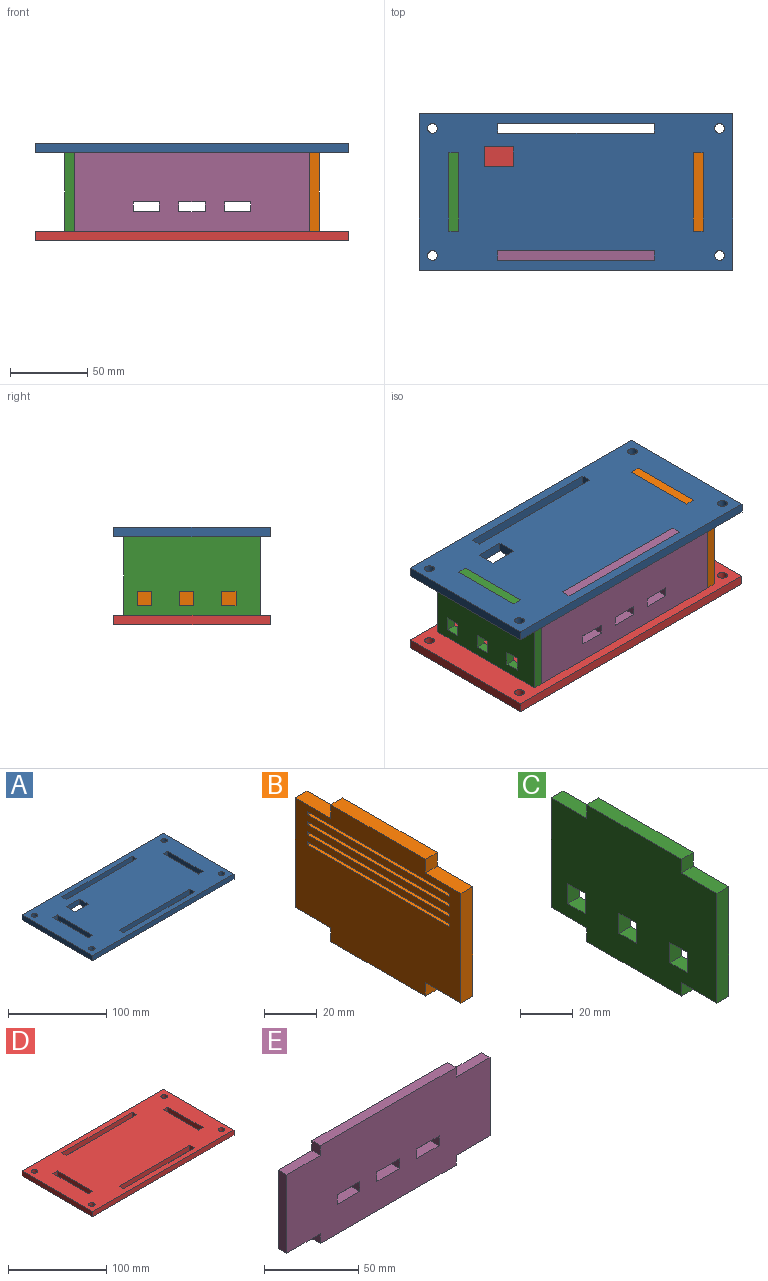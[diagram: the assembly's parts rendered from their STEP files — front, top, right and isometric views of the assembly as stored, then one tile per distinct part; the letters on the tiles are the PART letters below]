
ASSEMBLY  parts=5 mates=4
PART A: 30 faces, bbox 203.2x101.6x6.4 mm
  f0: plane 6.35x6.35mm, normal (0,-1,0), area 40.3mm2, adj f1,f27,f28,f29
  f1: plane 50.8x6.35mm, normal (-1,0,0), area 322.6mm2, adj f0,f2,f28,f29
  f2: plane 6.35x6.35mm, normal (0,1,0), area 40.3mm2, adj f1,f27,f28,f29
  f3: plane 101.6x6.35mm, normal (0,-1,0), area 645.2mm2, adj f4,f18,f28,f29
  f4: plane 6.35x6.35mm, normal (-1,0,0), area 40.3mm2, adj f3,f5,f28,f29
  f5: plane 101.6x6.35mm, normal (0,1,0), area 645.2mm2, adj f4,f18,f28,f29
  f6: plane 12.7x6.35mm, normal (1,0,0), area 80.6mm2, adj f7,f23,f28,f29
  f7: plane 19.05x6.35mm, normal (0,-1,0), area 121mm2, adj f6,f8,f28,f29
  f8: plane 12.7x6.35mm, normal (-1,0,0), area 80.6mm2, adj f7,f23,f28,f29
  f9: plane 6.35x6.35mm, normal (1,0,0), area 40.3mm2, adj f10,f24,f28,f29
  f10: plane 101.6x6.35mm, normal (0,-1,0), area 645.2mm2, adj f9,f11,f28,f29
  f11: plane 6.35x6.35mm, normal (-1,0,0), area 40.3mm2, adj f10,f24,f28,f29
  f12: plane 50.8x6.35mm, normal (1,0,0), area 322.6mm2, adj f13,f25,f28,f29
  f13: plane 6.35x6.35mm, normal (0,-1,0), area 40.3mm2, adj f12,f14,f28,f29
  f14: plane 50.8x6.35mm, normal (-1,0,0), area 322.6mm2, adj f13,f25,f28,f29
  f15: plane 101.6x6.35mm, normal (-1,0,0), area 645.2mm2, adj f16,f26,f28,f29
  f16: plane 203.2x6.35mm, normal (0,-1,0), area 1290.3mm2, adj f15,f17,f28,f29
  f17: plane 101.6x6.35mm, normal (1,0,0), area 645.2mm2, adj f16,f26,f28,f29
  f18: plane 6.35x6.35mm, normal (1,0,0), area 40.3mm2, adj f3,f5,f28,f29
  f19: cylinder r=3.17mm len=6.35mm, axis (0,0,-1), area 126.7mm2, adj f28,f29
  f20: cylinder r=3.17mm len=6.35mm, axis (0,0,-1), area 126.7mm2, adj f28,f29
  f21: cylinder r=3.17mm len=6.35mm, axis (0,0,-1), area 126.7mm2, adj f28,f29
  f22: cylinder r=3.17mm len=6.35mm, axis (0,0,-1), area 126.7mm2, adj f28,f29
  f23: plane 19.05x6.35mm, normal (0,1,0), area 121mm2, adj f6,f8,f28,f29
  f24: plane 101.6x6.35mm, normal (0,1,0), area 645.2mm2, adj f9,f11,f28,f29
  f25: plane 6.35x6.35mm, normal (0,1,0), area 40.3mm2, adj f12,f14,f28,f29
  f26: plane 203.2x6.35mm, normal (0,1,0), area 1290.3mm2, adj f15,f17,f28,f29
  f27: plane 50.8x6.35mm, normal (1,0,0), area 322.6mm2, adj f0,f2,f28,f29
  f28: plane 203.2x101.6mm, normal (0,0,1), area 18341mm2, adj f0,f1,f2,f3,f4,f5,f6,f7
  f29: plane 203.2x101.6mm, normal (0,0,-1), area 18341mm2, adj f0,f1,f2,f3,f4,f5,f6,f7
PART B: 30 faces, bbox 6.4x88.9x63.5 mm
  f0: plane 50.8x6.35mm, normal (0,-1,0), area 322.6mm2, adj f1,f27,f28,f29
  f1: plane 19.05x6.35mm, normal (0,0,-1), area 121mm2, adj f0,f2,f28,f29
  f2: plane 6.35x6.35mm, normal (0,-1,0), area 40.3mm2, adj f1,f3,f28,f29
  f3: plane 50.8x6.35mm, normal (0,0,-1), area 322.6mm2, adj f2,f4,f28,f29
  f4: plane 6.35x6.35mm, normal (0,1,0), area 40.3mm2, adj f3,f5,f28,f29
  f5: plane 19.05x6.35mm, normal (0,0,-1), area 121mm2, adj f4,f6,f28,f29
  f6: plane 50.8x6.35mm, normal (0,1,0), area 322.6mm2, adj f5,f7,f28,f29
  f7: plane 19.05x6.35mm, normal (0,0,1), area 121mm2, adj f6,f8,f28,f29
  f8: plane 6.35x6.35mm, normal (0,1,0), area 40.3mm2, adj f7,f9,f28,f29
  f9: plane 50.8x6.35mm, normal (0,0,1), area 322.6mm2, adj f8,f10,f28,f29
  f10: plane 6.35x6.35mm, normal (0,-1,0), area 40.3mm2, adj f9,f27,f28,f29
  f11: plane 6.35x1.5mm, normal (0,1,0), area 9.5mm2, adj f12,f23,f28,f29
  f12: plane 76.2x6.35mm, normal (0,0,-1), area 483.9mm2, adj f11,f13,f28,f29
  f13: plane 6.35x1.5mm, normal (0,-1,0), area 9.5mm2, adj f12,f23,f28,f29
  f14: plane 6.35x1.5mm, normal (0,1,0), area 9.5mm2, adj f15,f24,f28,f29
  f15: plane 76.2x6.35mm, normal (0,0,-1), area 483.9mm2, adj f14,f16,f28,f29
  f16: plane 6.35x1.5mm, normal (0,-1,0), area 9.5mm2, adj f15,f24,f28,f29
  f17: plane 6.35x1.5mm, normal (0,1,0), area 9.5mm2, adj f18,f25,f28,f29
  f18: plane 76.2x6.35mm, normal (0,0,-1), area 483.9mm2, adj f17,f19,f28,f29
  f19: plane 6.35x1.5mm, normal (0,-1,0), area 9.5mm2, adj f18,f25,f28,f29
  f20: plane 6.35x1.5mm, normal (0,1,0), area 9.5mm2, adj f21,f26,f28,f29
  f21: plane 76.2x6.35mm, normal (0,0,-1), area 483.9mm2, adj f20,f22,f28,f29
  f22: plane 6.35x1.5mm, normal (0,-1,0), area 9.5mm2, adj f21,f26,f28,f29
  f23: plane 76.2x6.35mm, normal (0,0,1), area 483.9mm2, adj f11,f13,f28,f29
  f24: plane 76.2x6.35mm, normal (0,0,1), area 483.9mm2, adj f14,f16,f28,f29
  f25: plane 76.2x6.35mm, normal (0,0,1), area 483.9mm2, adj f17,f19,f28,f29
  f26: plane 76.2x6.35mm, normal (0,0,1), area 483.9mm2, adj f20,f22,f28,f29
  f27: plane 19.05x6.35mm, normal (0,0,1), area 121mm2, adj f0,f10,f28,f29
  f28: plane 88.9x63.5mm, normal (-1,0,0), area 4705.6mm2, adj f0,f1,f2,f3,f4,f5,f6,f7
  f29: plane 88.9x63.5mm, normal (1,0,0), area 4705.6mm2, adj f0,f1,f2,f3,f4,f5,f6,f7
PART C: 26 faces, bbox 6.4x88.9x63.5 mm
  f0: plane 6.35x6.35mm, normal (0,1,0), area 40.3mm2, adj f1,f23,f24,f25
  f1: plane 50.8x6.35mm, normal (0,0,1), area 322.6mm2, adj f0,f2,f24,f25
  f2: plane 6.35x6.35mm, normal (0,-1,0), area 40.3mm2, adj f1,f3,f24,f25
  f3: plane 19.05x6.35mm, normal (0,0,1), area 121mm2, adj f2,f4,f24,f25
  f4: plane 50.8x6.35mm, normal (0,-1,0), area 322.6mm2, adj f3,f5,f24,f25
  f5: plane 19.05x6.35mm, normal (0,0,-1), area 121mm2, adj f4,f6,f24,f25
  f6: plane 6.35x6.35mm, normal (0,-1,0), area 40.3mm2, adj f5,f7,f24,f25
  f7: plane 50.8x6.35mm, normal (0,0,-1), area 322.6mm2, adj f6,f8,f24,f25
  f8: plane 6.35x6.35mm, normal (0,1,0), area 40.3mm2, adj f7,f9,f24,f25
  f9: plane 19.05x6.35mm, normal (0,0,-1), area 121mm2, adj f8,f10,f24,f25
  f10: plane 50.8x6.35mm, normal (0,1,0), area 322.6mm2, adj f9,f23,f24,f25
  f11: plane 9.38x6.35mm, normal (0,0,-1), area 59.6mm2, adj f12,f20,f24,f25
  f12: plane 9.38x6.35mm, normal (0,-1,0), area 59.6mm2, adj f11,f13,f24,f25
  f13: plane 9.38x6.35mm, normal (0,0,1), area 59.6mm2, adj f12,f20,f24,f25
  f14: plane 9.38x6.35mm, normal (0,0,-1), area 59.6mm2, adj f15,f21,f24,f25
  f15: plane 9.38x6.35mm, normal (0,-1,0), area 59.6mm2, adj f14,f16,f24,f25
  f16: plane 9.38x6.35mm, normal (0,0,1), area 59.6mm2, adj f15,f21,f24,f25
  f17: plane 9.38x6.35mm, normal (0,0,-1), area 59.6mm2, adj f18,f22,f24,f25
  f18: plane 9.38x6.35mm, normal (0,-1,0), area 59.6mm2, adj f17,f19,f24,f25
  f19: plane 9.38x6.35mm, normal (0,0,1), area 59.6mm2, adj f18,f22,f24,f25
  f20: plane 9.38x6.35mm, normal (0,1,0), area 59.6mm2, adj f11,f13,f24,f25
  f21: plane 9.38x6.35mm, normal (0,1,0), area 59.6mm2, adj f14,f16,f24,f25
  f22: plane 9.38x6.35mm, normal (0,1,0), area 59.6mm2, adj f17,f19,f24,f25
  f23: plane 19.05x6.35mm, normal (0,0,1), area 121mm2, adj f0,f10,f24,f25
  f24: plane 88.9x63.5mm, normal (1,0,0), area 4897.4mm2, adj f0,f1,f2,f3,f4,f5,f6,f7
  f25: plane 88.9x63.5mm, normal (-1,0,0), area 4897.4mm2, adj f0,f1,f2,f3,f4,f5,f6,f7
PART D: 26 faces, bbox 203.2x101.6x6.4 mm
  f0: plane 6.35x6.35mm, normal (0,-1,0), area 40.3mm2, adj f1,f23,f24,f25
  f1: plane 50.8x6.35mm, normal (-1,0,0), area 322.6mm2, adj f0,f2,f24,f25
  f2: plane 6.35x6.35mm, normal (0,1,0), area 40.3mm2, adj f1,f23,f24,f25
  f3: plane 101.6x6.35mm, normal (0,-1,0), area 645.2mm2, adj f4,f15,f24,f25
  f4: plane 6.35x6.35mm, normal (-1,0,0), area 40.3mm2, adj f3,f5,f24,f25
  f5: plane 101.6x6.35mm, normal (0,1,0), area 645.2mm2, adj f4,f15,f24,f25
  f6: plane 6.35x6.35mm, normal (1,0,0), area 40.3mm2, adj f7,f20,f24,f25
  f7: plane 101.6x6.35mm, normal (0,-1,0), area 645.2mm2, adj f6,f8,f24,f25
  f8: plane 6.35x6.35mm, normal (-1,0,0), area 40.3mm2, adj f7,f20,f24,f25
  f9: plane 50.8x6.35mm, normal (1,0,0), area 322.6mm2, adj f10,f21,f24,f25
  f10: plane 6.35x6.35mm, normal (0,-1,0), area 40.3mm2, adj f9,f11,f24,f25
  f11: plane 50.8x6.35mm, normal (-1,0,0), area 322.6mm2, adj f10,f21,f24,f25
  f12: plane 101.6x6.35mm, normal (-1,0,0), area 645.2mm2, adj f13,f22,f24,f25
  f13: plane 203.2x6.35mm, normal (0,-1,0), area 1290.3mm2, adj f12,f14,f24,f25
  f14: plane 101.6x6.35mm, normal (1,0,0), area 645.2mm2, adj f13,f22,f24,f25
  f15: plane 6.35x6.35mm, normal (1,0,0), area 40.3mm2, adj f3,f5,f24,f25
  f16: cylinder r=3.17mm len=6.35mm, axis (0,0,-1), area 126.7mm2, adj f24,f25
  f17: cylinder r=3.17mm len=6.35mm, axis (0,0,-1), area 126.7mm2, adj f24,f25
  f18: cylinder r=3.17mm len=6.35mm, axis (0,0,-1), area 126.7mm2, adj f24,f25
  f19: cylinder r=3.17mm len=6.35mm, axis (0,0,-1), area 126.7mm2, adj f24,f25
  f20: plane 101.6x6.35mm, normal (0,1,0), area 645.2mm2, adj f6,f8,f24,f25
  f21: plane 6.35x6.35mm, normal (0,1,0), area 40.3mm2, adj f9,f11,f24,f25
  f22: plane 203.2x6.35mm, normal (0,1,0), area 1290.3mm2, adj f12,f14,f24,f25
  f23: plane 50.8x6.35mm, normal (1,0,0), area 322.6mm2, adj f0,f2,f24,f25
  f24: plane 203.2x101.6mm, normal (0,0,1), area 18583mm2, adj f0,f1,f2,f3,f4,f5,f6,f7
  f25: plane 203.2x101.6mm, normal (0,0,-1), area 18583mm2, adj f0,f1,f2,f3,f4,f5,f6,f7
PART E: 26 faces, bbox 152.4x6.4x63.5 mm
  f0: plane 50.8x6.35mm, normal (-1,0,0), area 322.6mm2, adj f1,f23,f24,f25
  f1: plane 25.4x6.35mm, normal (0,0,-1), area 161.3mm2, adj f0,f2,f24,f25
  f2: plane 6.35x6.35mm, normal (-1,0,0), area 40.3mm2, adj f1,f3,f24,f25
  f3: plane 101.6x6.35mm, normal (0,0,-1), area 645.2mm2, adj f2,f4,f24,f25
  f4: plane 6.35x6.35mm, normal (1,0,0), area 40.3mm2, adj f3,f5,f24,f25
  f5: plane 25.4x6.35mm, normal (0,0,-1), area 161.3mm2, adj f4,f6,f24,f25
  f6: plane 50.8x6.35mm, normal (1,0,0), area 322.6mm2, adj f5,f7,f24,f25
  f7: plane 25.4x6.35mm, normal (0,0,1), area 161.3mm2, adj f6,f8,f24,f25
  f8: plane 6.35x6.35mm, normal (1,0,0), area 40.3mm2, adj f7,f9,f24,f25
  f9: plane 101.6x6.35mm, normal (0,0,1), area 645.2mm2, adj f8,f10,f24,f25
  f10: plane 6.35x6.35mm, normal (-1,0,0), area 40.3mm2, adj f9,f23,f24,f25
  f11: plane 6.35x6.35mm, normal (1,0,0), area 40.3mm2, adj f12,f20,f24,f25
  f12: plane 16.93x6.35mm, normal (0,0,-1), area 107.5mm2, adj f11,f13,f24,f25
  f13: plane 6.35x6.35mm, normal (-1,0,0), area 40.3mm2, adj f12,f20,f24,f25
  f14: plane 6.35x6.35mm, normal (1,0,0), area 40.3mm2, adj f15,f21,f24,f25
  f15: plane 16.93x6.35mm, normal (0,0,-1), area 107.5mm2, adj f14,f16,f24,f25
  f16: plane 6.35x6.35mm, normal (-1,0,0), area 40.3mm2, adj f15,f21,f24,f25
  f17: plane 6.35x6.35mm, normal (1,0,0), area 40.3mm2, adj f18,f22,f24,f25
  f18: plane 16.93x6.35mm, normal (0,0,-1), area 107.5mm2, adj f17,f19,f24,f25
  f19: plane 6.35x6.35mm, normal (-1,0,0), area 40.3mm2, adj f18,f22,f24,f25
  f20: plane 16.93x6.35mm, normal (0,0,1), area 107.5mm2, adj f11,f13,f24,f25
  f21: plane 16.93x6.35mm, normal (0,0,1), area 107.5mm2, adj f14,f16,f24,f25
  f22: plane 16.93x6.35mm, normal (0,0,1), area 107.5mm2, adj f17,f19,f24,f25
  f23: plane 25.4x6.35mm, normal (0,0,1), area 161.3mm2, adj f0,f10,f24,f25
  f24: plane 152.4x63.5mm, normal (0,-1,0), area 8709.7mm2, adj f0,f1,f2,f3,f4,f5,f6,f7
  f25: plane 152.4x63.5mm, normal (0,1,0), area 8709.7mm2, adj f0,f1,f2,f3,f4,f5,f6,f7
PLACE A t=(132.52,128.75,123.4)mm
PLACE B t=(-179.39,102.36,152.9)mm
PLACE C t=(-39.69,107.44,228.57)mm
PLACE D rot(axis=(0,0.97,0.25),0deg) t=(-132.3,117.11,148.8)mm
PLACE E rot(axis=(0,1,0),0deg) t=(96.3,79.01,155.15)mm
MATE fastened C.f1 <-> A.f28  axis (0,0,1) through (-208.5,91.71,212.3)mm
MATE fastened A.f28 <-> B.f9  axis (0,0,1) through (-56.1,142.51,212.3)mm
MATE fastened E.f9 <-> A.f28  axis (0,0,1) through (-81.5,79.01,212.3)mm
MATE fastened E.f3 <-> D.f25  axis (0,0,-1) through (-81.5,72.66,148.8)mm
